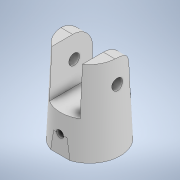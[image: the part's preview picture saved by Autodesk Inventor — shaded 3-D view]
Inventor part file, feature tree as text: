
AUTODESK INVENTOR PART (.ipt)
format: ipt  version: 2021 (Build 250183000, 183)  size: 249,344 bytes
history: native  units: mm
features: sketch x9, extrude x8, other x7, plane x2, fillet x1
ambient origin geometry x8: Origin, YZ Plane, XZ Plane, XY Plane, X Axis, Y Axis, Z Axis, Center Point
bodies: Volumenkörper1 (feature_tree), Volumenkörper5 (feature_tree), Volumenkörper7 (feature_tree), Volumenkörper8 (feature_tree), Volumenkörper9 (feature_tree), Volumenkörper10 (feature_tree)
feature tree (27):
  extrude  "Extrusion1"  Depth=27.0mm TaperAngle=0.0deg
  other  "Flächenverjüngung1"
  extrude  "Extrusion2"  Depth=10.0mm
  extrude  "Extrusion3"  Depth=3.5mm
  extrude  "Extrusion9"  Depth=30.0mm TaperAngle=0.0deg
  fillet  "Rundung3"  Radius=6.5mm
  other  "Kombinieren2"
  extrude  "Extrusion10"  Depth=6.0mm
  other  "Kombinieren4"
  extrude  "Extrusion11"  Depth=9.5mm TaperAngle=0.0deg
  other  "Kombinieren5"
  plane  "Arbeitsebene1"
  extrude  "Extrusion12"  Depth=6.0mm
  other  "Kombinieren6"
  extrude  "Extrusion13"  Depth=4.0mm
  other  "Kombinieren7"
  plane  "Arbeitsebene3"
  other  "Prägen1"
  sketch  "Skizze1"  dims[d6=20.0mm d7=27.0mm d8=0.0mm]
  sketch  "Skizze2"  dims[d12=15.0mm d13=0.0mm d14=10.0mm]
  sketch  "Skizze3"  dims[d15=5.0mm d16=3.5mm]
  sketch  "Skizze5"  dims[d18=30.0mm d19=0.0mm d42=30.0mm d43=0.0mm d44=6.5mm]
  sketch  "Skizze7"  dims[d46=7.25mm d47=6.0mm]
  sketch  "Skizze8"  dims[d48=9.5mm d49=40.0mm d50=0.0mm]
  sketch  "Skizze9"  dims[d51=-0.436332mm d52=6.0mm]
  sketch  "Skizze10"  dims[d53=0.0mm d54=4.0mm]
  sketch  "Skizze11"  dims[d55=2.0mm d56=22.25mm d57=0.0mm d58=3.5mm d60=2.4mm d61=6.0mm d63=22.25mm d64=0.0mm d66=0.0mm d67=3.0mm d68=3.0mm d69=0.0mm d70=0.0mm d71=2.5mm d72=2.5mm d73=10.0mm d74=0.0mm d76=-10.0mm d77=3.5mm d78=3.0mm d79=1.45mm d80=3.0mm d81=0.5mm d82=0.0mm d17=0.872665mm d37=0.5mm d38=0.872665mm d39=0.5mm d40=0.872665mm d59=0.872665mm]
